# Revit family: Gripple Universal Clamp with M8 Adaptor
name_source: partatom
category: Specialty Equipment
revit_build: Autodesk Revit 2017 (Build: 20160225_1515(x64)
units: mm (PartAtom-declared; Revit-internal decimal feet)

## family parameters
Always vertical = No
Cut with Voids When Loaded = No
OmniClass Number = 23.45.00.00
OmniClass Title = Sanitary, Laundry, and Cleaning Equipment
Part Type = Normal
Room Calculation Point = No
Round Connector Dimension = Use Diameter
Shared = No
Work Plane-Based = Yes

## types (2) — shared parameters
-width/2 = -15 mm  [stored -0.0492126 ft]
CAF = 13 mm  [stored 0.0426509 ft]
H = 22 mm
Manufacturer = Gripple Ltd
URL = http://www.gripple.co.uk
W = 30 mm  [stored 0.0984252 ft]
W/2 = 15 mm  [stored 0.0492126 ft]
zero-valued in all types: Cost, Default Elevation

## per-type parameters (varying)
| type | Assembly Code | Model |
| GUC M8/M10 400mm | GC2-INS-M8-M10-400MM | Gripple Universal Clamp - 400mm Wire |
| GUC M8/M10 600mm | GC2-INS-M8-M10-600MM | Gripple Universal Clamp - 600mm Wire |

note: [stored X ft] marks values corroborated as IEEE doubles in the binary element streams (Revit-internal decimal feet)

## geometry (parser evidence)
native form markers: Blend x2, Sweep x3
no freeform markers — native parametric forms only
